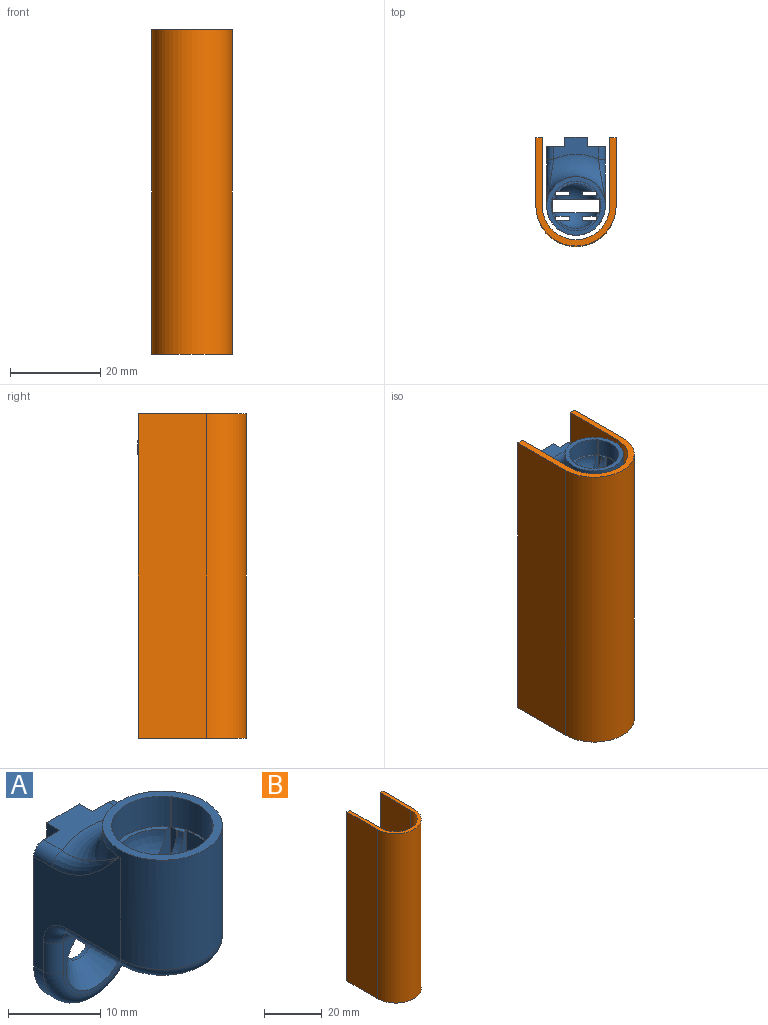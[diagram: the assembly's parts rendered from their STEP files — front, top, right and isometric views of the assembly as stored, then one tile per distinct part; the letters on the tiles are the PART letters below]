
ASSEMBLY  parts=2 mates=1
PART A: 62 faces, bbox 25x22.4x31.7 mm
  f0: plane 22.5x13mm, normal (0,1,0), area 245.8mm2, adj f33,f34,f35,f38,f39,f55,f57,f58
  f1: plane 9.54x3.5mm, normal (0,0,-1), area 19.2mm2, adj f14,f17,f19,f20,f30,f31,f32,f53
  f2: plane 6.32x1.04mm, normal (0,0,1), area 1.9mm2, adj f10,f14,f15,f16,f18,f19,f25,f28
  f3: plane 8.87x2.25mm, normal (0,0,1), area 4.7mm2, adj f11,f22,f26,f41
  f4: plane 6.32x1.04mm, normal (0,0,1), area 1.9mm2, adj f9,f13,f14,f15,f23,f24,f29,f32
  f5: plane 8.87x2.25mm, normal (0,0,1), area 4.7mm2, adj f12,f17,f30,f40
  f6: plane 10x6.8mm, normal (0,0,-1), area 61.5mm2, adj f15,f21,f22,f23,f24,f25,f26,f27
  f7: cylinder r=6.5mm len=14.5mm, axis (0,0,-1), area 316.5mm2, adj f8,f34,f35,f36,f53
  f8: plane 13x13mm, normal (0,0,1), area 37.7mm2, adj f7,f9,f10,f11,f12,f17,f18,f22
  f9: cylinder r=5.5mm len=6.32mm, axis (0,0,1), area 27mm2, adj f4,f8,f23,f29
  f10: cylinder r=5.5mm len=6.32mm, axis (0,0,1), area 27mm2, adj f2,f8,f18,f25
  f11: cylinder r=5.5mm len=8.87mm, axis (0,0,1), area 41.3mm2, adj f3,f8,f22,f26
  f12: cylinder r=5.5mm len=8.87mm, axis (0,0,1), area 41.3mm2, adj f5,f8,f17,f30
  f13: plane 11.98x3mm, normal (-1,0,0), area 35.9mm2, adj f4,f14,f15,f52,f53
  f14: plane 12.01x10.51mm, normal (0,1,0), area 90.2mm2, adj f1,f2,f4,f13,f16,f40,f53
  f15: plane 12x10.5mm, normal (0,-1,0), area 90.3mm2, adj f2,f4,f6,f13,f16,f41,f51,f52
  f16: plane 11.98x3mm, normal (1,0,0), area 35.9mm2, adj f2,f14,f15,f51,f53
  f17: plane 16.03x3.03mm, normal (0,1,0), area 30.4mm2, adj f1,f5,f8,f12,f18,f20,f40,f53
  f18: plane 16x1mm, normal (1,0,0), area 12.3mm2, adj f2,f8,f10,f17,f19,f53
  f19: plane 12x3mm, normal (0,-1,0), area 26.9mm2, adj f1,f2,f18,f20,f40,f53
  f20: plane 8.6x1.09mm, normal (-1,0,0), area 8.1mm2, adj f1,f17,f19,f40
  f21: plane 8.6x1.09mm, normal (1,0,0), area 8.1mm2, adj f6,f22,f24,f41
  f22: plane 16x3mm, normal (0,-1,0), area 30.5mm2, adj f3,f6,f8,f11,f21,f23,f41
  f23: plane 16x1mm, normal (-1,0,0), area 12.4mm2, adj f4,f6,f8,f9,f22,f24
  f24: plane 12x3mm, normal (0,1,0), area 26.9mm2, adj f4,f6,f21,f23,f41
  f25: plane 16x1mm, normal (1,0,0), area 12.4mm2, adj f2,f6,f8,f10,f26,f28
  f26: plane 16x3mm, normal (0,-1,0), area 30.5mm2, adj f3,f6,f8,f11,f25,f27,f41
  f27: plane 8.6x1.09mm, normal (-1,0,0), area 8.1mm2, adj f6,f26,f28,f41
  f28: plane 12x3mm, normal (0,1,0), area 26.9mm2, adj f2,f6,f25,f27,f41
  f29: plane 16x1mm, normal (-1,0,0), area 12.3mm2, adj f4,f8,f9,f30,f32,f53
  f30: plane 16.03x3.03mm, normal (0,1,0), area 30.4mm2, adj f1,f5,f8,f12,f29,f31,f40,f53
  f31: plane 8.6x1.09mm, normal (1,0,0), area 8.1mm2, adj f1,f30,f32,f40
  f32: plane 12x3mm, normal (0,-1,0), area 26.9mm2, adj f1,f4,f29,f31,f40,f53
  f33: plane 10x4.88mm, normal (0,0,1), area 31.1mm2, adj f0,f36,f55,f57,f58,f60,f61
  f34: plane 21x13.23mm, normal (1,0,0), area 129.1mm2, adj f0,f7,f38,f48,f50,f52,f56,f57
  f35: plane 21x13.23mm, normal (-1,0,0), area 129.1mm2, adj f0,f7,f38,f47,f49,f51,f54,f55
  f36: torus R=11.5mm, axis (0,0,-1), area 107.7mm2, adj f7,f33,f54,f56
  f37: plane 10x9mm, normal (0,-1,0), area 17mm2, adj f42,f43,f45,f46,f47,f48
  f38: cylinder r=6.5mm len=13mm, axis (0,1,0), area 30.6mm2, adj f0,f34,f35,f46
  f39: cylinder r=2mm len=4mm, axis (0,-1,0), area 6.3mm2, adj f0,f42
  f40: sphere r=5mm, area 43mm2, adj f2,f4,f5,f14,f17,f19,f20,f30
  f41: sphere r=5mm, area 43mm2, adj f2,f3,f4,f15,f21,f22,f24,f26
  f42: cone r=2mm half-angle=45deg, axis (0,-1,0), area 72.2mm2, adj f37,f39,f44
  f43: cylinder r=2mm len=2.94mm, axis (1,0,0), area 9.2mm2, adj f6,f37,f44,f49
  f44: bspline ~5.29x2.42mm, area 11.6mm2, adj f6,f42,f43,f45
  f45: cylinder r=2mm len=2.94mm, axis (1,0,0), area 9.2mm2, adj f6,f37,f44,f50
  f46: torus R=5mm, axis (0,1,0), area 44.1mm2, adj f37,f38,f47,f48
  f47: cylinder r=1.5mm len=4mm, axis (0,0,1), area 9.4mm2, adj f35,f37,f46,f49
  f48: cylinder r=1.5mm len=4mm, axis (0,0,-1), area 9.4mm2, adj f34,f37,f46,f50
  f49: torus R=3.5mm, axis (-1,0,0), area 9.4mm2, adj f35,f43,f47,f51
  f50: torus R=3.5mm, axis (-1,0,0), area 9.4mm2, adj f34,f45,f48,f52
  f51: cylinder r=1.5mm len=8.23mm, axis (0,-1,0), area 19mm2, adj f6,f15,f16,f35,f49,f53
  f52: cylinder r=1.5mm len=8.23mm, axis (0,1,0), area 19mm2, adj f6,f13,f15,f34,f50,f53
  f53: torus R=5mm, axis (0,0,1), area 42.4mm2, adj f1,f7,f13,f14,f16,f17,f18,f19
  f54: bspline ~10.36x6.5mm, area 16.2mm2, adj f35,f36,f55
  f55: cylinder r=1.5mm len=2.88mm, axis (0,-1,0), area 6.8mm2, adj f0,f33,f35,f54
  f56: bspline ~11.34x6.5mm, area 16.2mm2, adj f34,f36,f57
  f57: cylinder r=1.5mm len=2.88mm, axis (0,1,0), area 6.8mm2, adj f0,f33,f34,f56
  f58: plane 3x2mm, normal (1,0,0), area 6mm2, adj f0,f33,f59,f61
  f59: plane 5x2mm, normal (0,0,-1), area 10mm2, adj f0,f58,f60,f61
  f60: plane 3x2mm, normal (-1,0,0), area 6mm2, adj f0,f33,f59,f61
  f61: plane 5x3mm, normal (0,1,0), area 15mm2, adj f33,f58,f59,f60
PART B: 10 faces, bbox 17.8x24x72 mm
  f0: plane 72x15.1mm, normal (-1,0,0), area 1087.2mm2, adj f1,f7,f8,f9
  f1: cylinder r=8.9mm len=72mm, axis (0,0,-1), area 2013.1mm2, adj f0,f2,f8,f9
  f2: plane 72x15.1mm, normal (1,0,0), area 1087.2mm2, adj f1,f3,f8,f9
  f3: plane 72x1.4mm, normal (0,1,0), area 100.8mm2, adj f2,f4,f8,f9
  f4: plane 72x15.1mm, normal (-1,0,0), area 1087.2mm2, adj f3,f5,f8,f9
  f5: cylinder r=7.5mm len=72mm, axis (0,0,-1), area 1696.5mm2, adj f4,f6,f8,f9
  f6: plane 72x15.1mm, normal (1,0,0), area 1087.2mm2, adj f5,f7,f8,f9
  f7: plane 72x1.4mm, normal (0,1,0), area 100.8mm2, adj f0,f6,f8,f9
  f8: plane 24x17.8mm, normal (0,0,1), area 78.3mm2, adj f0,f1,f2,f3,f4,f5,f6,f7
  f9: plane 24x17.8mm, normal (0,0,-1), area 78.3mm2, adj f0,f1,f2,f3,f4,f5,f6,f7
PLACE A t=(-9.66,-8.8,-0.04)mm fixed
PLACE B t=(-9.66,-8.8,-56.04)mm
MATE parallel A.f9 <-> B.f5  axis (0,0,1) through (-9.66,-8.8,15.96)mm
